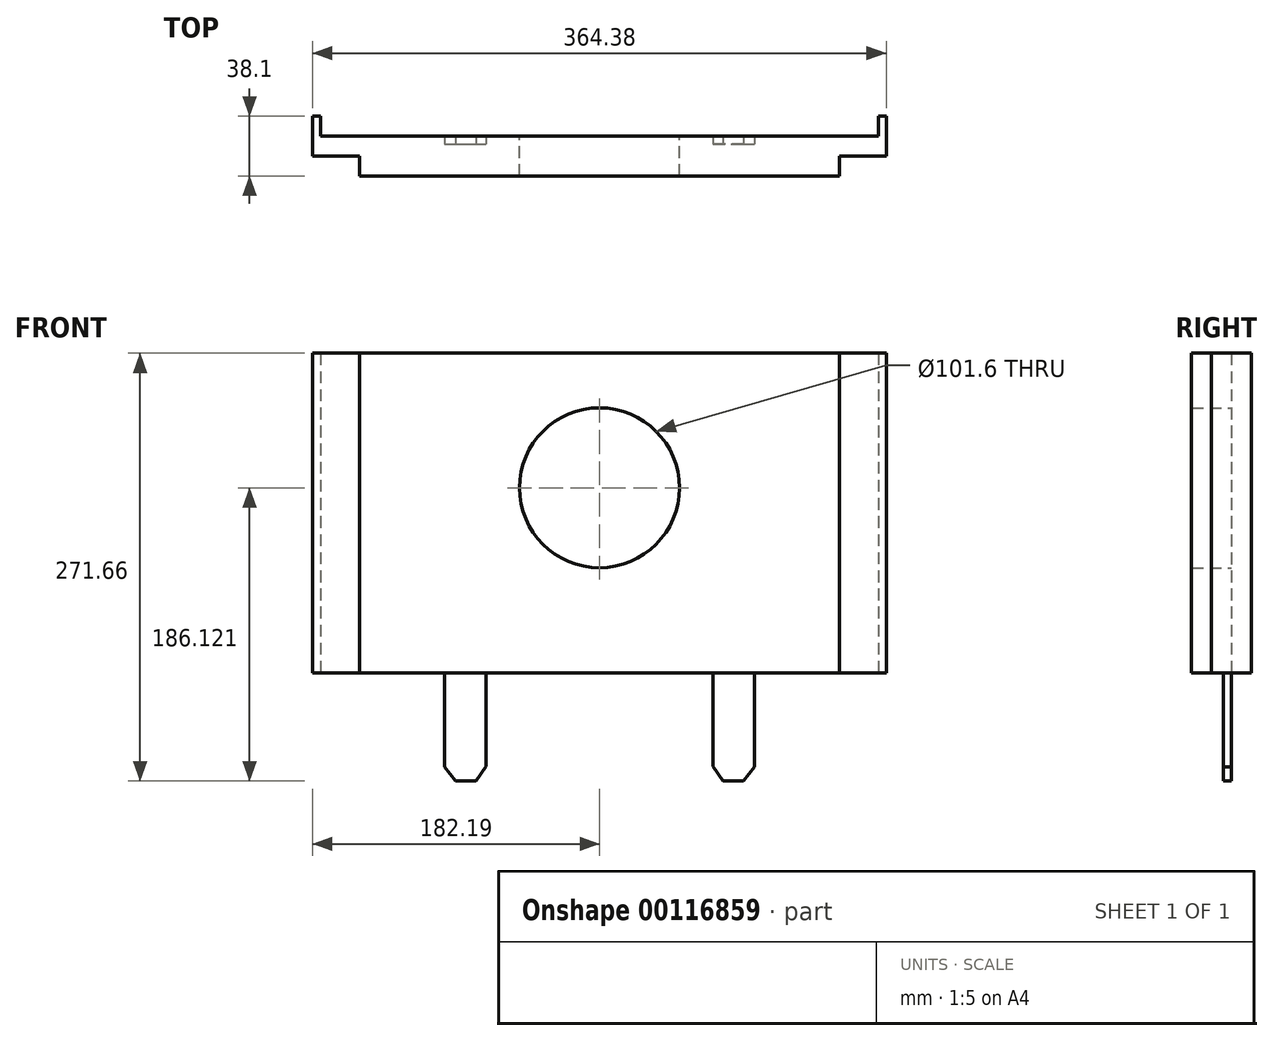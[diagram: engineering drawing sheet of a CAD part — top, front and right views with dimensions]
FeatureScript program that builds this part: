
annotation { "Feature Type Name" : "Feature", "Feature Type Description" : "" }
export const myFeature = defineFeature(function(context is Context, id is Id, definition is map)
    precondition{}
    {
        {
            var Q0;
            Q0=qCreatedBy(makeId("Front.planeOp"),FACE);
            var sketch = newSketch(context, id + "F0", { "sketchPlane" : qUnion([Q0])});
            skLineSegment(sketch, "E0", {"start": v(-152.4, 76.8) * mm, "end": v(-152.4, -126.4) * mm});
            skLineSegment(sketch, "E1", {"start": v(-152.4, -126.4) * mm, "end": v(0, -126.4) * mm});
            skLineSegment(sketch, "E2", {"start": v(-152.4, 76.8) * mm, "end": v(0, 76.8) * mm});
            skLineSegment(sketch, "E3.MirrorCS", {"start": v(152.4, 76.8) * mm, "end": v(152.4, -126.4) * mm});
            skLineSegment(sketch, "E4.MirrorCS", {"start": v(152.4, 76.8) * mm, "end": v(0, 76.8) * mm});
            skLineSegment(sketch, "E5.MirrorCS", {"start": v(152.4, -126.4) * mm, "end": v(0, -126.4) * mm});
            skSolve(sketch);
        }
        {
            var Q0;
            Q0=makeQuery(id+"F0.imprint","IMPRINT",FACE,{"disambiguationData":[TD([[makeQuery(id+"F0.imprint","IMPRINT",EDGE,{"derivedFrom":sQuery(id+"F0.wireOp",EDGE,"E0")}),1.0]])]});
            extrude(context, id + "F1", {"entities" : qUnion([Q0]), "depth" : 25.4 * mm});
        }
        {
            var Q0;
            Q0=makeQuery(id+"F1.opExtrude","CAP_FACE",FACE,{"disambiguationData":[OSD([sQuery(id+"F0.wireOp",EDGE,"E0"),sQuery(id+"F0.wireOp",EDGE,"E1"),sQuery(id+"F0.wireOp",EDGE,"E2"),sQuery(id+"F0.wireOp",EDGE,"E3.MirrorCS"),sQuery(id+"F0.wireOp",EDGE,"E4.MirrorCS"),sQuery(id+"F0.wireOp",EDGE,"E5.MirrorCS")])],"isStart":false});
            var sketch = newSketch(context, id + "F2", { "sketchPlane" : qUnion([Q0])});
            skLineSegment(sketch, "E6", {"start": v(-98.46, -126.4) * mm, "end": v(-98.46, -185.86) * mm});
            skLineSegment(sketch, "E7", {"start": v(-98.46, -185.86) * mm, "end": v(-91.54, -194.86) * mm});
            skLineSegment(sketch, "E8", {"start": v(-91.54, -194.86) * mm, "end": v(-78.37, -194.86) * mm});
            skLineSegment(sketch, "E9", {"start": v(-78.37, -194.86) * mm, "end": v(-72.14, -185.6) * mm});
            skLineSegment(sketch, "E10", {"start": v(-98.46, -185.86) * mm, "end": v(-72.14, -185.6) * mm});
            skLineSegment(sketch, "E11", {"start": v(-72.14, -185.6) * mm, "end": v(-72.14, -126.4) * mm});
            skLineSegment(sketch, "E12.MirrorCS", {"start": v(72.14, -185.6) * mm, "end": v(72.14, -126.4) * mm});
            skLineSegment(sketch, "E13.MirrorCS", {"start": v(98.46, -126.4) * mm, "end": v(98.46, -185.86) * mm});
            skLineSegment(sketch, "E14.MirrorCS", {"start": v(98.46, -185.86) * mm, "end": v(72.14, -185.6) * mm});
            skLineSegment(sketch, "E15.MirrorCS", {"start": v(78.37, -194.86) * mm, "end": v(72.14, -185.6) * mm});
            skLineSegment(sketch, "E16.MirrorCS", {"start": v(91.54, -194.86) * mm, "end": v(78.37, -194.86) * mm});
            skLineSegment(sketch, "E17", {"start": v(91.54, -194.86) * mm, "end": v(98.46, -185.86) * mm});
            skLineSegment(sketch, "E18", {"start": v(-98.46, -126.4) * mm, "end": v(-72.14, -126.4) * mm});
            skLineSegment(sketch, "E19", {"start": v(72.14, -126.4) * mm, "end": v(98.46, -126.4) * mm});
            skSolve(sketch);
        }
        {
            var Q0;
            Q0 = qSketchRegion(id + "F2", true);
            extrude(context, id + "F3", {"entities" : qUnion([Q0]), "operationType" : NewBodyOperationType.ADD, "oppositeDirection" : true, "depth" : 25.4 * mm, "hasSecondDirection" : true, "secondDirectionOppositeDirection" : true, "secondDirectionDepth" : 20.32 * mm});
        }
        {
            var Q0;
            Q0=makeQuery(id+"F1.opExtrude","CAP_FACE",FACE,{"disambiguationData":[OSD([sQuery(id+"F0.wireOp",EDGE,"E0"),sQuery(id+"F0.wireOp",EDGE,"E1"),sQuery(id+"F0.wireOp",EDGE,"E2"),sQuery(id+"F0.wireOp",EDGE,"E3.MirrorCS"),sQuery(id+"F0.wireOp",EDGE,"E4.MirrorCS"),sQuery(id+"F0.wireOp",EDGE,"E5.MirrorCS")])],"isStart":true});
            var sketch = newSketch(context, id + "F4", { "sketchPlane" : qUnion([Q0])});
            skLineSegment(sketch, "E20.bottom", {"start": v(-139.01, 76.8) * mm, "end": v(-182.2, 76.8) * mm});
            skLineSegment(sketch, "E20.top", {"start": v(-139.01, -126.4) * mm, "end": v(-182.2, -126.4) * mm});
            skLineSegment(sketch, "E20.left", {"start": v(-139.01, 76.8) * mm, "end": v(-139.01, -126.4) * mm});
            skLineSegment(sketch, "E20.right", {"start": v(-182.2, 76.8) * mm, "end": v(-182.2, -126.4) * mm});
            skLineSegment(sketch, "E21.MirrorCS", {"start": v(139.01, 76.8) * mm, "end": v(139.01, -126.4) * mm});
            skLineSegment(sketch, "E22.MirrorCS", {"start": v(139.01, 76.8) * mm, "end": v(182.2, 76.8) * mm});
            skLineSegment(sketch, "E23.MirrorCS", {"start": v(182.2, 76.8) * mm, "end": v(182.2, -126.4) * mm});
            skLineSegment(sketch, "E24.MirrorCS", {"start": v(139.01, -126.4) * mm, "end": v(182.2, -126.4) * mm});
            skSolve(sketch);
        }
        {
            var Q0;
            Q0 = qSketchRegion(id + "F4", true);
            extrude(context, id + "F5", {"entities" : qUnion([Q0]), "operationType" : NewBodyOperationType.ADD, "oppositeDirection" : true, "depth" : 12.7 * mm});
        }
        {
            var Q0;
            Q0=makeQuery(id+"F5.boolean.opBoolean","MERGE",FACE,{"derivedFrom":[makeQuery(id+"F1.opExtrude","CAP_FACE",FACE,{"disambiguationData":[OSD([sQuery(id+"F0.wireOp",EDGE,"E0"),sQuery(id+"F0.wireOp",EDGE,"E1"),sQuery(id+"F0.wireOp",EDGE,"E2"),sQuery(id+"F0.wireOp",EDGE,"E3.MirrorCS"),sQuery(id+"F0.wireOp",EDGE,"E4.MirrorCS"),sQuery(id+"F0.wireOp",EDGE,"E5.MirrorCS")])],"isStart":true}),makeQuery(id+"F5.opExtrude","CAP_FACE",FACE,{"disambiguationData":[OSD([sQuery(id+"F4.wireOp",EDGE,"E20.bottom"),sQuery(id+"F4.wireOp",EDGE,"E20.top"),sQuery(id+"F4.wireOp",EDGE,"E20.left"),sQuery(id+"F4.wireOp",EDGE,"E20.right")])],"isStart":true}),makeQuery(id+"F5.opExtrude","CAP_FACE",FACE,{"disambiguationData":[OSD([sQuery(id+"F4.wireOp",EDGE,"E21.MirrorCS"),sQuery(id+"F4.wireOp",EDGE,"E22.MirrorCS"),sQuery(id+"F4.wireOp",EDGE,"E23.MirrorCS"),sQuery(id+"F4.wireOp",EDGE,"E24.MirrorCS")])],"isStart":true})]});
            var sketch = newSketch(context, id + "F6", { "sketchPlane" : qUnion([Q0])});
            skLineSegment(sketch, "E25.bottom", {"start": v(-177.11, 76.8) * mm, "end": v(-182.2, 76.8) * mm});
            skLineSegment(sketch, "E25.top", {"start": v(-177.11, -126.4) * mm, "end": v(-182.2, -126.4) * mm});
            skLineSegment(sketch, "E25.left", {"start": v(-177.11, 76.8) * mm, "end": v(-177.11, -126.4) * mm});
            skLineSegment(sketch, "E25.right", {"start": v(-182.2, 76.8) * mm, "end": v(-182.2, -126.4) * mm});
            skLineSegment(sketch, "E26.MirrorCS", {"start": v(177.11, 76.8) * mm, "end": v(177.11, -126.4) * mm});
            skLineSegment(sketch, "E27.MirrorCS", {"start": v(177.11, 76.8) * mm, "end": v(182.2, 76.8) * mm});
            skLineSegment(sketch, "E28.MirrorCS", {"start": v(182.2, 76.8) * mm, "end": v(182.2, -126.4) * mm});
            skLineSegment(sketch, "E29.MirrorCS", {"start": v(177.11, -126.4) * mm, "end": v(182.2, -126.4) * mm});
            skSolve(sketch);
        }
        {
            var Q0;
            Q0 = qSketchRegion(id + "F6", true);
            extrude(context, id + "F7", {"entities" : qUnion([Q0]), "operationType" : NewBodyOperationType.ADD, "depth" : 12.7 * mm});
        }
        {
            var Q0;
            Q0=makeQuery(id+"F5.boolean.opBoolean","MERGE",FACE,{"derivedFrom":[makeQuery(id+"F3.boolean.opBoolean","MERGE",FACE,{"derivedFrom":[makeQuery(id+"F1.opExtrude","CAP_FACE",FACE,{"disambiguationData":[OSD([sQuery(id+"F0.wireOp",EDGE,"E0"),sQuery(id+"F0.wireOp",EDGE,"E1"),sQuery(id+"F0.wireOp",EDGE,"E2"),sQuery(id+"F0.wireOp",EDGE,"E3.MirrorCS"),sQuery(id+"F0.wireOp",EDGE,"E4.MirrorCS"),sQuery(id+"F0.wireOp",EDGE,"E5.MirrorCS")])],"isStart":true}),makeQuery(id+"F3.opExtrude","CAP_FACE",FACE,{"disambiguationData":[OSD([sQuery(id+"F2.wireOp",EDGE,"E6"),sQuery(id+"F2.wireOp",EDGE,"E7"),sQuery(id+"F2.wireOp",EDGE,"E8"),sQuery(id+"F2.wireOp",EDGE,"E9"),sQuery(id+"F2.wireOp",EDGE,"E11"),sQuery(id+"F2.wireOp",EDGE,"E18")])],"isStart":false}),makeQuery(id+"F3.opExtrude","CAP_FACE",FACE,{"disambiguationData":[OSD([sQuery(id+"F2.wireOp",EDGE,"E12.MirrorCS"),sQuery(id+"F2.wireOp",EDGE,"E13.MirrorCS"),sQuery(id+"F2.wireOp",EDGE,"E15.MirrorCS"),sQuery(id+"F2.wireOp",EDGE,"E16.MirrorCS"),sQuery(id+"F2.wireOp",EDGE,"E17"),sQuery(id+"F2.wireOp",EDGE,"E19")])],"isStart":false})]}),makeQuery(id+"F5.opExtrude","CAP_FACE",FACE,{"disambiguationData":[OSD([sQuery(id+"F4.wireOp",EDGE,"E20.bottom"),sQuery(id+"F4.wireOp",EDGE,"E20.top"),sQuery(id+"F4.wireOp",EDGE,"E20.left"),sQuery(id+"F4.wireOp",EDGE,"E20.right")])],"isStart":true}),makeQuery(id+"F5.opExtrude","CAP_FACE",FACE,{"disambiguationData":[OSD([sQuery(id+"F4.wireOp",EDGE,"E21.MirrorCS"),sQuery(id+"F4.wireOp",EDGE,"E22.MirrorCS"),sQuery(id+"F4.wireOp",EDGE,"E23.MirrorCS"),sQuery(id+"F4.wireOp",EDGE,"E24.MirrorCS")])],"isStart":true})]});
            var sketch = newSketch(context, id + "F8", { "sketchPlane" : qUnion([Q0])});
            skCircle(sketch, "E30", {"center": v(0, -8.74) * mm, "radius": 50.8 * mm});
            skSolve(sketch);
        }
        {
            var Q0;
            Q0=makeQuery(id+"F8.imprint","IMPRINT",FACE,{"disambiguationData":[TD([[makeQuery(id+"F8.imprint","IMPRINT",EDGE,{"derivedFrom":sQuery(id+"F8.wireOp",EDGE,"E30")}),1.0]])]});
            extrude(context, id + "F9", {"entities" : qUnion([Q0]), "operationType" : NewBodyOperationType.REMOVE, "oppositeDirection" : true, "depth" : 25.4 * mm});
        }
    });
